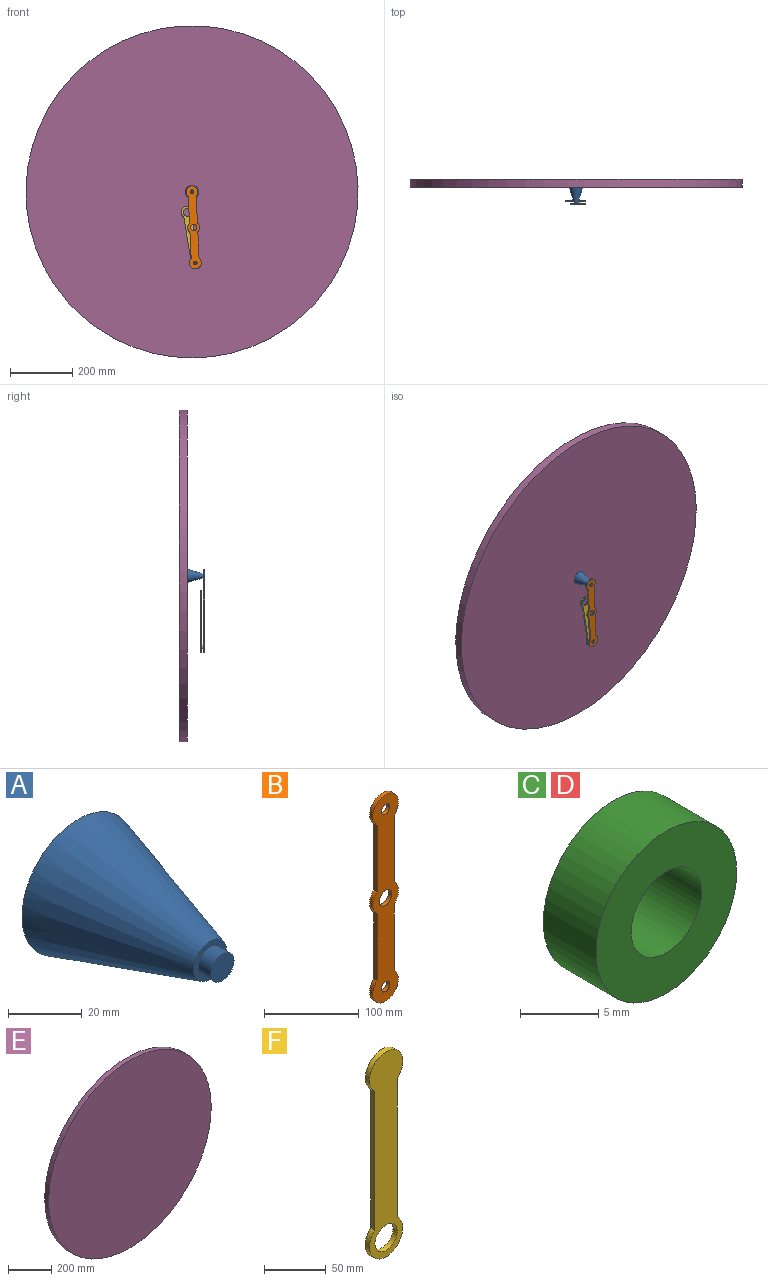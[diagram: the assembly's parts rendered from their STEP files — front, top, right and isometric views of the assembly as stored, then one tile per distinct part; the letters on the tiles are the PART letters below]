
ASSEMBLY  parts=6 mates=5
PART A: 5 faces, bbox 43.2x55.6x43.2 mm
  f0: plane 12.7x12.7mm, normal (0,-1,0), area 64.6mm2, adj f2,f4
  f1: plane 43.18x43.18mm, normal (0,1,0), area 1464.4mm2, adj f4
  f2: cylinder r=4.45mm len=8.89mm, axis (0,1,0), area 133mm2, adj f0,f3
  f3: plane 8.89x8.89mm, normal (0,-1,0), area 62.1mm2, adj f2
  f4: cone r=6.35mm half-angle=16.7deg, axis (0,1,0), area 4655.4mm2, adj f0,f1
PART B: 13 faces, bbox 38.1x4.8x266.9 mm
  f0: plane 85.9x4.76mm, normal (1,0,0), area 409.1mm2, adj f1,f9,f11,f12
  f1: cylinder r=19.05mm len=38.1mm, axis (0,1,0), area 437.6mm2, adj f0,f2,f11,f12
  f2: plane 85.9x4.76mm, normal (-1,0,0), area 409.1mm2, adj f1,f3,f11,f12
  f3: cylinder r=19.05mm len=28.4mm, axis (0,1,0), area 152.6mm2, adj f2,f4,f11,f12
  f4: plane 86.15x4.76mm, normal (-1,0,0), area 410.3mm2, adj f3,f5,f11,f12
  f5: cylinder r=19.05mm len=38.1mm, axis (0,1,0), area 437.6mm2, adj f4,f6,f11,f12
  f6: plane 86.15x4.76mm, normal (1,0,0), area 410.3mm2, adj f5,f9,f11,f12
  f7: cylinder r=9.53mm len=19.05mm, axis (0,1,0), area 285mm2, adj f11,f12
  f8: cylinder r=6.35mm len=12.7mm, axis (0,1,0), area 190mm2, adj f11,f12
  f9: cylinder r=19.05mm len=28.4mm, axis (0,1,0), area 152.6mm2, adj f0,f6,f11,f12
  f10: cylinder r=6.35mm len=12.7mm, axis (0,1,0), area 190mm2, adj f11,f12
  f11: plane 266.95x38.1mm, normal (0,-1,0), area 6914mm2, adj f0,f1,f2,f3,f4,f5,f6,f7
  f12: plane 266.95x38.1mm, normal (0,1,0), area 6914mm2, adj f0,f1,f2,f3,f4,f5,f6,f7
PART C: 4 faces, bbox 12.7x4.8x12.7 mm
  f0: cylinder r=3.17mm len=6.35mm, axis (0,1,0), area 95mm2, adj f2,f3
  f1: cylinder r=6.35mm len=12.7mm, axis (0,1,0), area 190mm2, adj f2,f3
  f2: plane 12.7x12.7mm, normal (0,-1,0), area 95mm2, adj f0,f1
  f3: plane 12.7x12.7mm, normal (0,1,0), area 95mm2, adj f0,f1
PART D: same geometry as C
PART E: 3 faces, bbox 1066.8x25.4x1066.8 mm
  f0: cylinder r=533.4mm len=1066.8mm, axis (0,1,0), area 85126.9mm2, adj f1,f2
  f1: plane 1066.8x1066.8mm, normal (0,-1,0), area 893832mm2, adj f0
  f2: plane 1066.8x1066.8mm, normal (0,1,0), area 893832mm2, adj f0
PART F: 13 faces, bbox 38.1x14.3x203.3 mm
  f0: plane 136.79x4.76mm, normal (1,0,0), area 651.5mm2, adj f1,f3,f5,f6
  f1: cylinder r=19.05mm len=38.1mm, axis (0,1,0), area 437.6mm2, adj f0,f2,f5,f6
  f2: plane 136.79x4.76mm, normal (-1,0,0), area 651.5mm2, adj f1,f3,f5,f6
  f3: cylinder r=19.05mm len=38.1mm, axis (0,1,0), area 437.6mm2, adj f0,f2,f5,f6
  f4: cylinder r=12.7mm len=25.4mm, axis (0,1,0), area 380mm2, adj f5,f6
  f5: plane 203.29x38.1mm, normal (0,-1,0), area 5079mm2, adj f0,f1,f2,f3,f4
  f6: plane 203.29x38.1mm, normal (0,1,0), area 4952.3mm2, adj f0,f1,f2,f3,f4,f7,f8
  f7: cylinder r=6.35mm len=12.7mm, axis (0,-1,0), area 95mm2, adj f6,f8,f9
  f8: extruded ~12.7x6.35mm, area 95mm2, adj f6,f7,f9
  f9: plane 14.61x12.7mm, normal (0,1,0), area 64.6mm2, adj f7,f8,f11,f12
  f10: plane 10.22x8.89mm, normal (0,1,0), area 62.1mm2, adj f11,f12
  f11: cylinder r=4.45mm len=8.89mm, axis (0,-1,0), area 66.5mm2, adj f9,f10,f12
  f12: extruded ~8.89x4.76mm, area 66.5mm2, adj f9,f10,f11
PLACE A t=(22.14,10.78,-194.45)mm
PLACE B rot(axis=(0,1,0),177.3deg) t=(32.75,-40.02,-423.05)mm
PLACE C t=(22.14,-40.02,-194.45)mm
PLACE D t=(32.75,-40.02,-423.05)mm
PLACE E t=(22.14,36.18,-194.45)mm
PLACE F rot(axis=(1,0,0.08),180deg) t=(32.75,-35.26,-423.05)mm
MATE revolute B.f10 <-> C.f1  axis (0,-1,0) through (22.14,-44.78,-194.45)mm
MATE revolute D.f0 <-> B.f8  axis (0,-1,0) through (32.75,-44.78,-423.05)mm
MATE revolute F.f11 <-> B.f8  axis (0,-1,0) through (32.75,-44.78,-423.05)mm
MATE fastened E.f0 <-> A.f4  axis (0,-1,0) through (22.14,10.78,-194.45)mm
MATE revolute C.f0 <-> A.f2  axis (0,-1,0) through (22.14,-44.78,-194.45)mm
